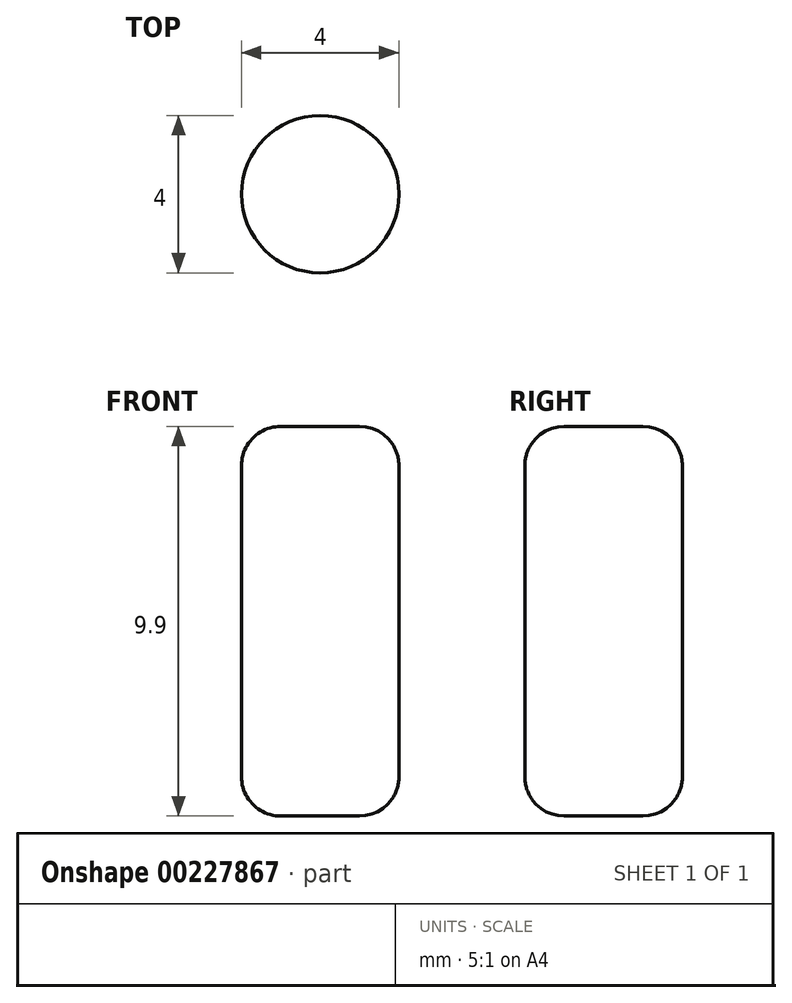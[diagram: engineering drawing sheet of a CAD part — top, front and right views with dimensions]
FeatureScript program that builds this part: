
annotation { "Feature Type Name" : "Feature", "Feature Type Description" : "" }
export const myFeature = defineFeature(function(context is Context, id is Id, definition is map)
    precondition{}
    {
        {
            var Q0;
            Q0=qCreatedBy(makeId("Front.planeOp"),FACE);
            var sketch = newSketch(context, id + "F0", { "sketchPlane" : qUnion([Q0])});
            skLineSegment(sketch, "E0.bottom", {"start": v(0, 0) * mm, "end": v(-1, 0) * mm});
            skLineSegment(sketch, "E0.top", {"start": v(0, 9.9) * mm, "end": v(-1, 9.9) * mm});
            skLineSegment(sketch, "E0.left", {"start": v(0, 0) * mm, "end": v(0, 9.9) * mm});
            skLineSegment(sketch, "E0.right", {"start": v(-2, 1) * mm, "end": v(-2, 8.9) * mm});
            skPoint(sketch, "E1.visualSharp", {"position": v(-2, 9.9) * mm});
            skArc(sketch, "E1.filletArc", {"start": v(-1, 9.9) * mm, "mid": v(-1.7, 9.6) * mm, "end": v(-2, 8.9) * mm});
            skPoint(sketch, "E2.visualSharp", {"position": v(-2, 0) * mm});
            skArc(sketch, "E2.filletArc", {"start": v(-2, 1) * mm, "mid": v(-1.7, 0.3) * mm, "end": v(-1, 0) * mm});
            skSolve(sketch);
        }
        {
            var Q0;
            Q0=makeQuery(id+"F0.imprint","IMPRINT",FACE,{"disambiguationData":[TD([[makeQuery(id+"F0.imprint","IMPRINT",EDGE,{"derivedFrom":sQuery(id+"F0.wireOp",EDGE,"E0.bottom")}),-1.0]])]});
            var Q1;
            Q1=sQuery(id+"F0.wireOp",EDGE,"E0.left");
            revolve(context, id + "F1", {"entities" : qUnion([Q0]), "axis" : qUnion([Q1]), "revolveType" : RevolveType.FULL});
        }
    });
